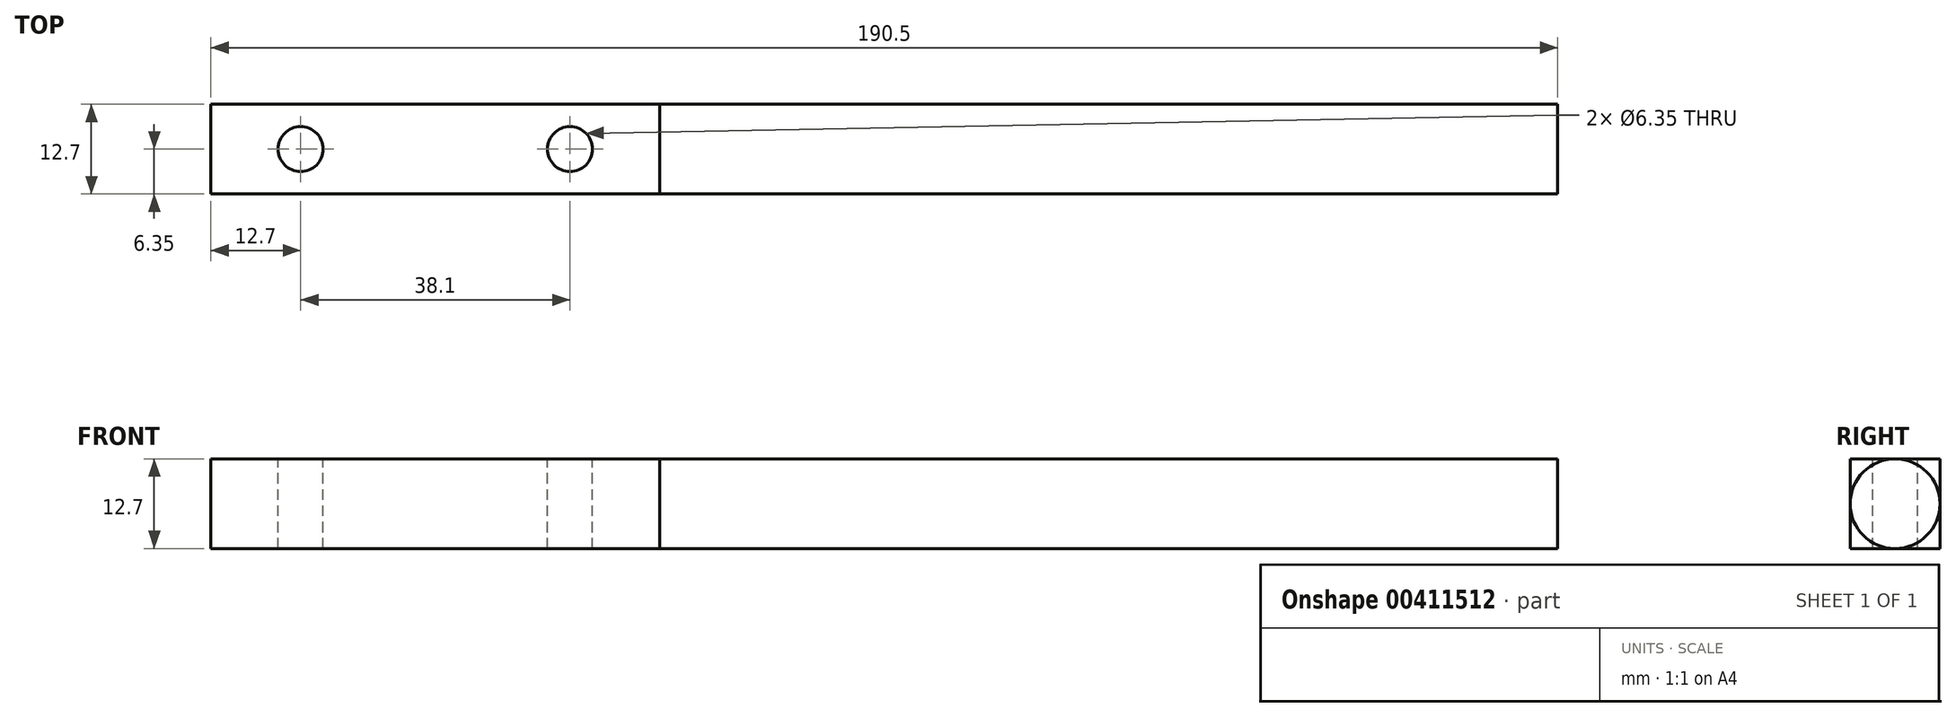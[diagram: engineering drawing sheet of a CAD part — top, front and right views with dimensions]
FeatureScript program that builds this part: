
annotation { "Feature Type Name" : "Feature", "Feature Type Description" : "" }
export const myFeature = defineFeature(function(context is Context, id is Id, definition is map)
    precondition{}
    {
        {
            var Q0;
            Q0=qCreatedBy(makeId("Right.planeOp"),FACE);
            var sketch = newSketch(context, id + "F0", { "sketchPlane" : qUnion([Q0])});
            skLineSegment(sketch, "E0.bottom", {"start": v(-6.35, 6.35) * mm, "end": v(6.35, 6.35) * mm});
            skLineSegment(sketch, "E0.top", {"start": v(-6.35, -6.35) * mm, "end": v(6.35, -6.35) * mm});
            skLineSegment(sketch, "E0.left", {"start": v(-6.35, 6.35) * mm, "end": v(-6.35, -6.35) * mm});
            skLineSegment(sketch, "E0.right", {"start": v(6.35, 6.35) * mm, "end": v(6.35, -6.35) * mm});
            skPoint(sketch, "E0.middle", {"position": v(0, 0) * mm});
            skSolve(sketch);
        }
        {
            var Q0;
            Q0 = qSketchRegion(id + "F0", true);
            extrude(context, id + "F1", {"entities" : qUnion([Q0]), "oppositeDirection" : true, "depth" : 63.5 * mm});
        }
        {
            var Q0;
            Q0=makeQuery(id+"F1.opExtrude","CAP_FACE",FACE,{"disambiguationData":[OSD([sQuery(id+"F0.wireOp",EDGE,"E0.bottom"),sQuery(id+"F0.wireOp",EDGE,"E0.top"),sQuery(id+"F0.wireOp",EDGE,"E0.left"),sQuery(id+"F0.wireOp",EDGE,"E0.right")])],"isStart":true});
            var sketch = newSketch(context, id + "F2", { "sketchPlane" : qUnion([Q0])});
            skCircle(sketch, "E1", {"center": v(0, 0) * mm, "radius": 6.35 * mm});
            skSolve(sketch);
        }
        {
            var Q0;
            Q0 = qSketchRegion(id + "F2", true);
            extrude(context, id + "F3", {"entities" : qUnion([Q0]), "operationType" : NewBodyOperationType.ADD, "depth" : 127 * mm});
        }
        {
            var Q0;
            Q0=makeQuery(id+"F1.opExtrude","SWEPT_FACE",FACE,{"disambiguationData":[OSD([sQuery(id+"F0.wireOp",EDGE,"E0.bottom")])]});
            var sketch = newSketch(context, id + "F4", { "sketchPlane" : qUnion([Q0])});
            skPoint(sketch, "E2", {"position": v(-50.8, 0) * mm});
            skPoint(sketch, "E3", {"position": v(-12.7, 0) * mm});
            skCircle(sketch, "E4", {"center": v(-50.8, 0) * mm, "radius": 3.18 * mm});
            skCircle(sketch, "E5", {"center": v(-12.7, 0) * mm, "radius": 3.18 * mm});
            skSolve(sketch);
        }
        {
            var Q0;
            Q0=makeQuery(id+"F4.imprint","IMPRINT",FACE,{"disambiguationData":[TD([[makeQuery(id+"F4.imprint","IMPRINT",EDGE,{"derivedFrom":sQuery(id+"F4.wireOp",EDGE,"E4")}),1.0]])]});
            var Q1;
            Q1=makeQuery(id+"F4.imprint","IMPRINT",FACE,{"disambiguationData":[TD([[makeQuery(id+"F4.imprint","IMPRINT",EDGE,{"derivedFrom":sQuery(id+"F4.wireOp",EDGE,"E5")}),1.0]])]});
            extrude(context, id + "F5", {"entities" : qUnion([Q0, Q1]), "operationType" : NewBodyOperationType.REMOVE, "endBound" : BoundingType.THROUGH_ALL, "oppositeDirection" : true, "depth" : 25.4 * mm});
        }
    });
